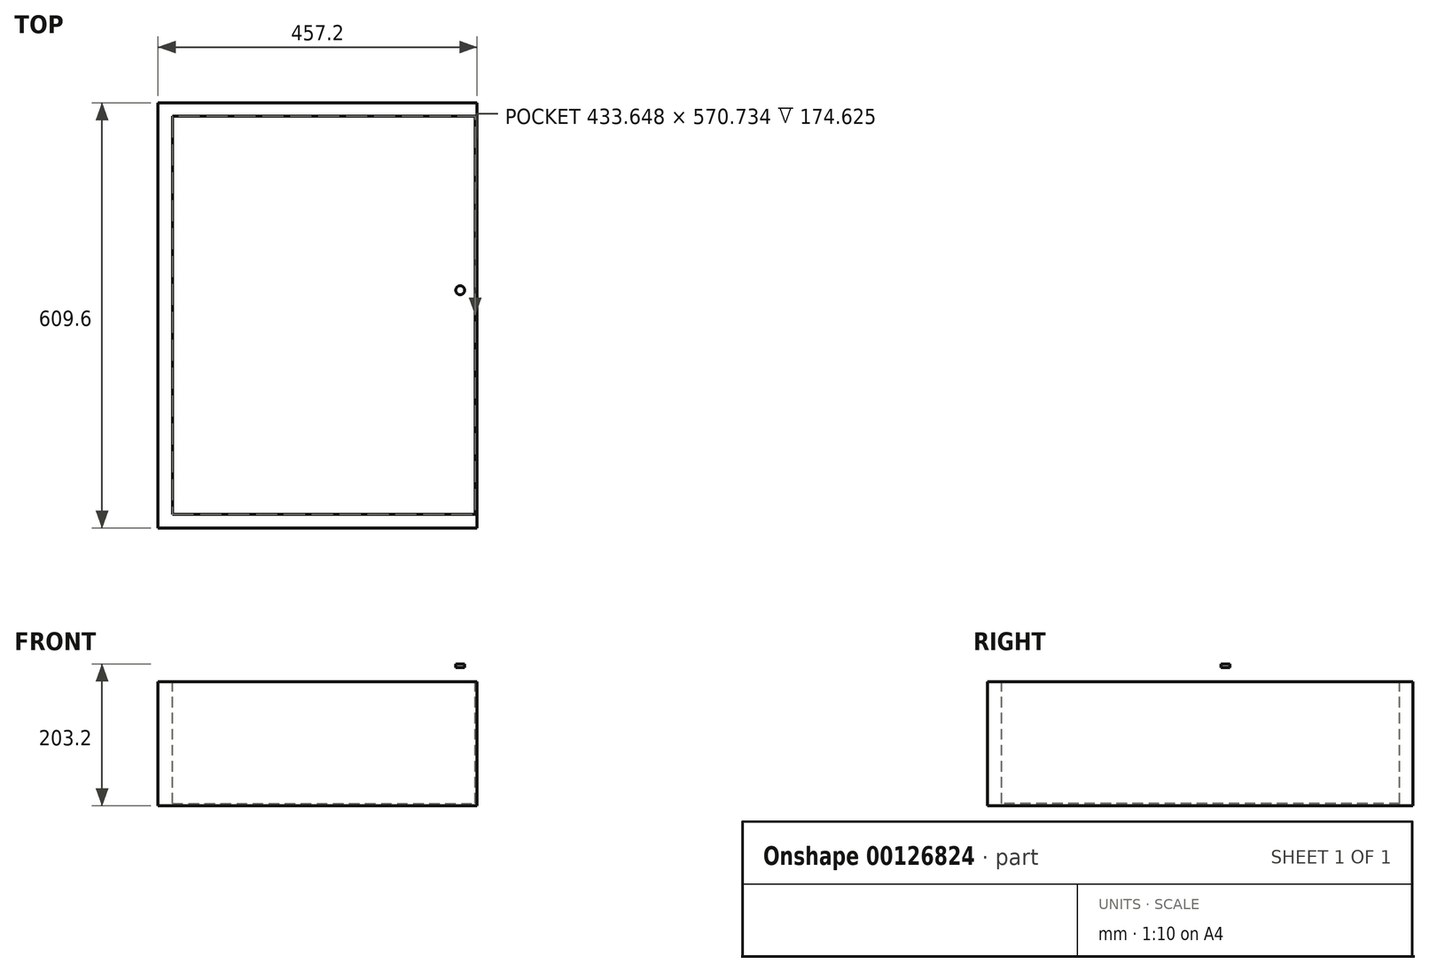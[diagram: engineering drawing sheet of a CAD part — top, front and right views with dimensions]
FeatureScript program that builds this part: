
annotation { "Feature Type Name" : "Feature", "Feature Type Description" : "" }
export const myFeature = defineFeature(function(context is Context, id is Id, definition is map)
    precondition{}
    {
        {
            var Q0;
            Q0=qCreatedBy(makeId("Top.planeOp"),FACE);
            var sketch = newSketch(context, id + "F0", { "sketchPlane" : qUnion([Q0])});
            skLineSegment(sketch, "E0.bottom", {"start": v(228.6, 304.8) * mm, "end": v(-228.6, 304.8) * mm});
            skLineSegment(sketch, "E0.top", {"start": v(228.6, -304.8) * mm, "end": v(-228.6, -304.8) * mm});
            skLineSegment(sketch, "E0.left", {"start": v(228.6, 304.8) * mm, "end": v(228.6, -304.8) * mm});
            skLineSegment(sketch, "E0.right", {"start": v(-228.6, 304.8) * mm, "end": v(-228.6, -304.8) * mm});
            skPoint(sketch, "E0.middle", {"position": v(0, 0) * mm});
            skSolve(sketch);
        }
        {
            var Q0;
            Q0=makeQuery(id+"F0.imprint","IMPRINT",FACE,{"disambiguationData":[TD([[makeQuery(id+"F0.imprint","IMPRINT",EDGE,{"derivedFrom":sQuery(id+"F0.wireOp",EDGE,"E0.bottom")}),1.0]])]});
            extrude(context, id + "F1", {"entities" : qUnion([Q0]), "depth" : 203.2 * mm});
        }
        {
            var Q0;
            Q0=makeQuery(id+"F1.opExtrude","CAP_FACE",FACE,{"disambiguationData":[OSD([sQuery(id+"F0.wireOp",EDGE,"E0.bottom"),sQuery(id+"F0.wireOp",EDGE,"E0.top"),sQuery(id+"F0.wireOp",EDGE,"E0.left"),sQuery(id+"F0.wireOp",EDGE,"E0.right")])],"isStart":false});
            var sketch = newSketch(context, id + "F2", { "sketchPlane" : qUnion([Q0])});
            skLineSegment(sketch, "E1.bottom", {"start": v(-207.94, 285.9) * mm, "end": v(180.25, 285.9) * mm});
            skLineSegment(sketch, "E1.top", {"start": v(-207.94, -284.84) * mm, "end": v(180.25, -284.84) * mm});
            skLineSegment(sketch, "E1.left", {"start": v(-207.94, 285.9) * mm, "end": v(-207.94, -284.84) * mm});
            skLineSegment(sketch, "E1.right", {"start": v(180.25, 285.9) * mm, "end": v(180.25, -284.84) * mm});
            skSolve(sketch);
        }
        {
            var Q0;
            Q0=makeQuery(id+"F2.imprint","IMPRINT",FACE,{"disambiguationData":[TD([[makeQuery(id+"F2.imprint","IMPRINT",EDGE,{"derivedFrom":sQuery(id+"F2.wireOp",EDGE,"E1.bottom")}),-1.0]])]});
            extrude(context, id + "F3", {"entities" : qUnion([Q0]), "operationType" : NewBodyOperationType.REMOVE, "oppositeDirection" : true, "depth" : 200.02 * mm});
        }
        {
            var Q0;
            Q0=makeQuery(id+"F3.boolean.opBoolean","COPY",FACE,{"derivedFrom":makeQuery(id+"F3.opExtrude","SWEPT_FACE",FACE,{"disambiguationData":[OSD([sQuery(id+"F2.wireOp",EDGE,"E1.right")])]})});
            var sketch = newSketch(context, id + "F4", { "sketchPlane" : qUnion([Q0])});
            skLineSegment(sketch, "E2", {"start": v(-285.9, 198.19) * mm, "end": v(284.84, 198.19) * mm});
            skSolve(sketch);
        }
        {
            var Q0;
            {var subQ0=sQuery(id+"F4.wireOp",EDGE,"E2");Q0=makeQuery(id+"F4.imprint","IMPRINT",FACE,{"disambiguationData":[TD([[makeQuery(id+"F4.imprint","IMPRINT",EDGE,{"derivedFrom":subQ0}),-1.0]])]});}
            extrude(context, id + "F5", {"entities" : qUnion([Q0]), "operationType" : NewBodyOperationType.REMOVE, "oppositeDirection" : true, "depth" : 45.46 * mm});
        }
        {
            var Q0;
            Q0=makeQuery(id+"F1.opExtrude","CAP_FACE",FACE,{"disambiguationData":[OSD([sQuery(id+"F0.wireOp",EDGE,"E0.bottom"),sQuery(id+"F0.wireOp",EDGE,"E0.top"),sQuery(id+"F0.wireOp",EDGE,"E0.left"),sQuery(id+"F0.wireOp",EDGE,"E0.right")])],"isStart":false});
            var sketch = newSketch(context, id + "F6", { "sketchPlane" : qUnion([Q0])});
            skCircle(sketch, "E3", {"center": v(204.42, 230.38) * mm, "radius": 6.35 * mm});
            skArc(sketch, "E4", {"start": v(210.77, 201.19) * mm, "mid": v(204.24, 207.53) * mm, "end": v(198.08, 200.82) * mm});
            skArc(sketch, "E5", {"start": v(198.07, 151.88) * mm, "mid": v(204.42, 145.53) * mm, "end": v(210.77, 151.88) * mm});
            skLineSegment(sketch, "E6", {"start": v(198.08, 200.82) * mm, "end": v(198.07, 151.88) * mm});
            skLineSegment(sketch, "E7", {"start": v(210.77, 201.19) * mm, "end": v(210.77, 151.88) * mm});
            skCircle(sketch, "E8.MirrorC", {"center": v(204.42, 36.16) * mm, "radius": 6.35 * mm});
            skLineSegment(sketch, "E9.MirrorCS", {"start": v(198.08, 65.73) * mm, "end": v(198.07, 114.66) * mm});
            skLineSegment(sketch, "E10.MirrorCS", {"start": v(210.77, 65.36) * mm, "end": v(210.77, 114.66) * mm});
            skArc(sketch, "E11.MirrorCS", {"start": v(210.77, 65.36) * mm, "mid": v(204.24, 59.01) * mm, "end": v(198.08, 65.73) * mm});
            skArc(sketch, "E12.MirrorCS", {"start": v(198.07, 114.66) * mm, "mid": v(204.42, 121.01) * mm, "end": v(210.77, 114.66) * mm});
            skSolve(sketch);
        }
        {
            var Q0;
            Q0=makeQuery(id+"F6.imprint","IMPRINT",FACE,{"disambiguationData":[TD([[makeQuery(id+"F6.imprint","IMPRINT",EDGE,{"derivedFrom":sQuery(id+"F6.wireOp",EDGE,"E3")}),1.0]])]});
            var Q1;
            Q1=makeQuery(id+"F6.imprint","IMPRINT",FACE,{"disambiguationData":[TD([[makeQuery(id+"F6.imprint","IMPRINT",EDGE,{"derivedFrom":sQuery(id+"F6.wireOp",EDGE,"E4")}),1.0]])]});
            var Q2;
            Q2=makeQuery(id+"F6.imprint","IMPRINT",FACE,{"disambiguationData":[TD([[makeQuery(id+"F6.imprint","IMPRINT",EDGE,{"derivedFrom":sQuery(id+"F6.wireOp",EDGE,"E9.MirrorCS")}),-1.0]])]});
            var Q3;
            Q3=makeQuery(id+"F6.imprint","IMPRINT",FACE,{"disambiguationData":[TD([[makeQuery(id+"F6.imprint","IMPRINT",EDGE,{"derivedFrom":sQuery(id+"F6.wireOp",EDGE,"E8.MirrorC")}),-1.0]])]});
            extrude(context, id + "F7", {"entities" : qUnion([Q0, Q1, Q2, Q3]), "operationType" : NewBodyOperationType.REMOVE, "oppositeDirection" : true, "depth" : 25.4 * mm});
        }
    });
